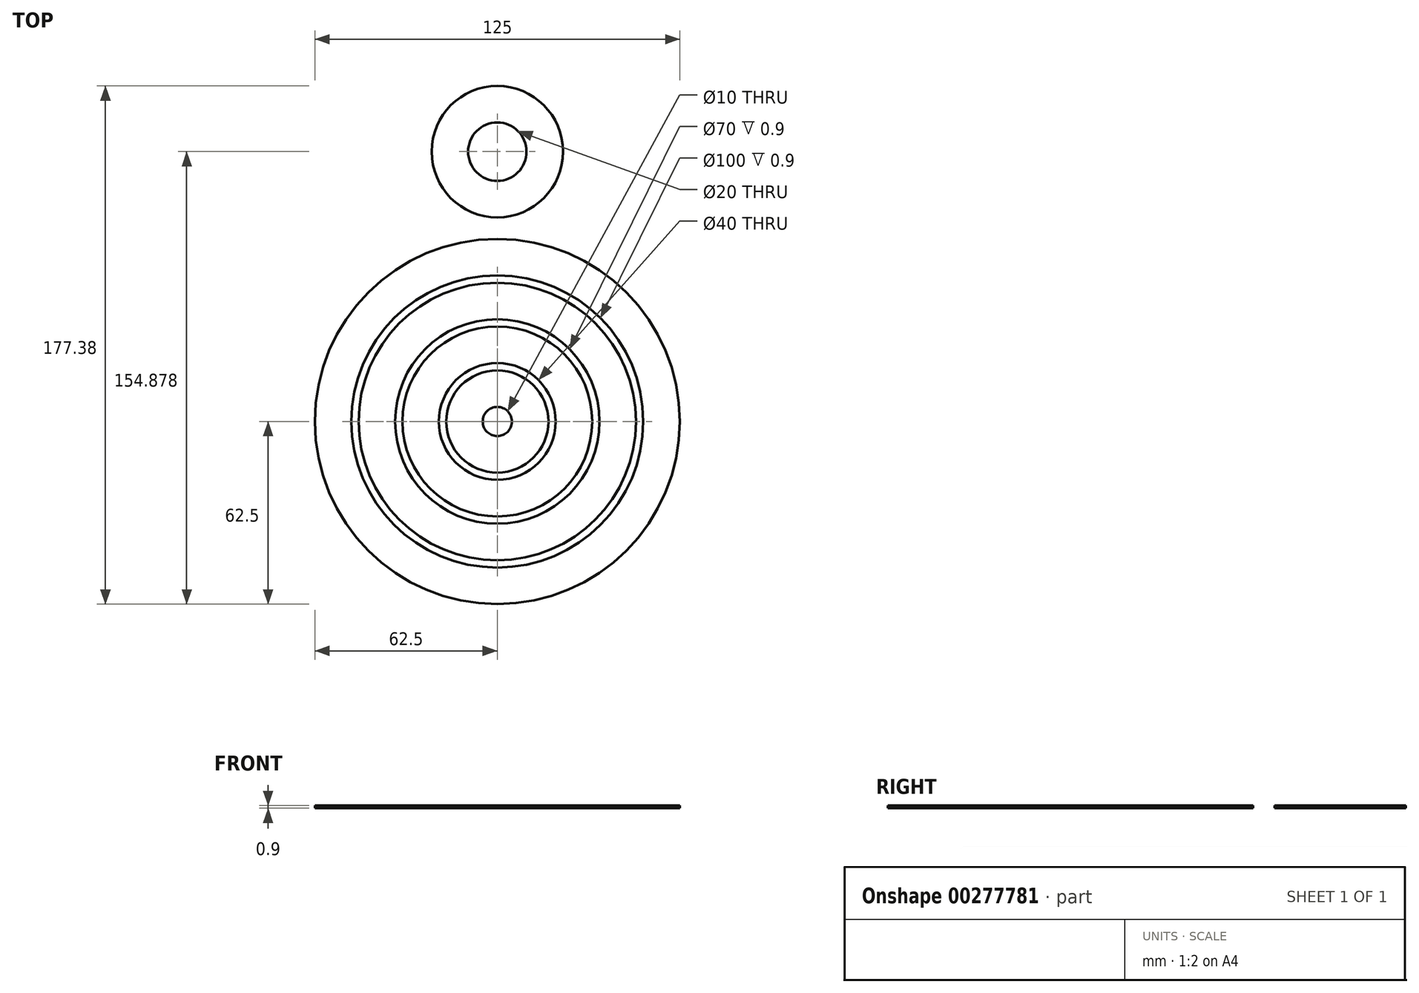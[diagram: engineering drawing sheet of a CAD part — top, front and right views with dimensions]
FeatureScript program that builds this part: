
annotation { "Feature Type Name" : "Feature", "Feature Type Description" : "" }
export const myFeature = defineFeature(function(context is Context, id is Id, definition is map)
    precondition{}
    {
        {
            var Q0;
            Q0=qCreatedBy(makeId("Top.planeOp"),FACE);
            var sketch = newSketch(context, id + "F0", { "sketchPlane" : qUnion([Q0])});
            skCircle(sketch, "E0", {"center": v(0, 0) * mm, "radius": 62.5 * mm});
            skCircle(sketch, "E1", {"center": v(0, 0) * mm, "radius": 50 * mm});
            skCircle(sketch, "E2", {"center": v(0, 0) * mm, "radius": 47.5 * mm});
            skCircle(sketch, "E3", {"center": v(0, 0) * mm, "radius": 35 * mm});
            skCircle(sketch, "E4", {"center": v(0, 0) * mm, "radius": 32.5 * mm});
            skCircle(sketch, "E5", {"center": v(0, 0) * mm, "radius": 20 * mm});
            skCircle(sketch, "E6", {"center": v(0, 0) * mm, "radius": 17.5 * mm});
            skCircle(sketch, "E7", {"center": v(0, 0) * mm, "radius": 5 * mm});
            skCircle(sketch, "E8", {"center": v(0, 92.38) * mm, "radius": 22.5 * mm});
            skCircle(sketch, "E9", {"center": v(0, 92.38) * mm, "radius": 10 * mm});
            skSolve(sketch);
        }
        {
            var Q0;
            Q0=makeQuery(id+"F0.imprint","IMPRINT",FACE,{"disambiguationData":[TD([[makeQuery(id+"F0.imprint","IMPRINT",EDGE,{"derivedFrom":sQuery(id+"F0.wireOp",EDGE,"E0")}),1.0]])]});
            var Q1;
            Q1=makeQuery(id+"F0.imprint","IMPRINT",FACE,{"disambiguationData":[TD([[makeQuery(id+"F0.imprint","IMPRINT",EDGE,{"derivedFrom":sQuery(id+"F0.wireOp",EDGE,"E2")}),1.0]])]});
            var Q2;
            Q2=makeQuery(id+"F0.imprint","IMPRINT",FACE,{"disambiguationData":[TD([[makeQuery(id+"F0.imprint","IMPRINT",EDGE,{"derivedFrom":sQuery(id+"F0.wireOp",EDGE,"E4")}),1.0]])]});
            var Q3;
            Q3=makeQuery(id+"F0.imprint","IMPRINT",FACE,{"disambiguationData":[TD([[makeQuery(id+"F0.imprint","IMPRINT",EDGE,{"derivedFrom":sQuery(id+"F0.wireOp",EDGE,"E6")}),1.0]])]});
            var Q4;
            Q4=makeQuery(id+"F0.imprint","IMPRINT",FACE,{"disambiguationData":[TD([[makeQuery(id+"F0.imprint","IMPRINT",EDGE,{"derivedFrom":sQuery(id+"F0.wireOp",EDGE,"E8")}),1.0]])]});
            var Q5;
            Q5=sQuery(id+"F0.wireOp",EDGE,"E0");
            var Q6;
            Q6=sQuery(id+"F0.wireOp",EDGE,"E1");
            extrude(context, id + "F1", {"entities" : qUnion([Q0, Q1, Q2, Q3, Q4]), "surfaceEntities" : qUnion([Q5, Q6]), "depth" : 0.9 * mm});
        }
    });
